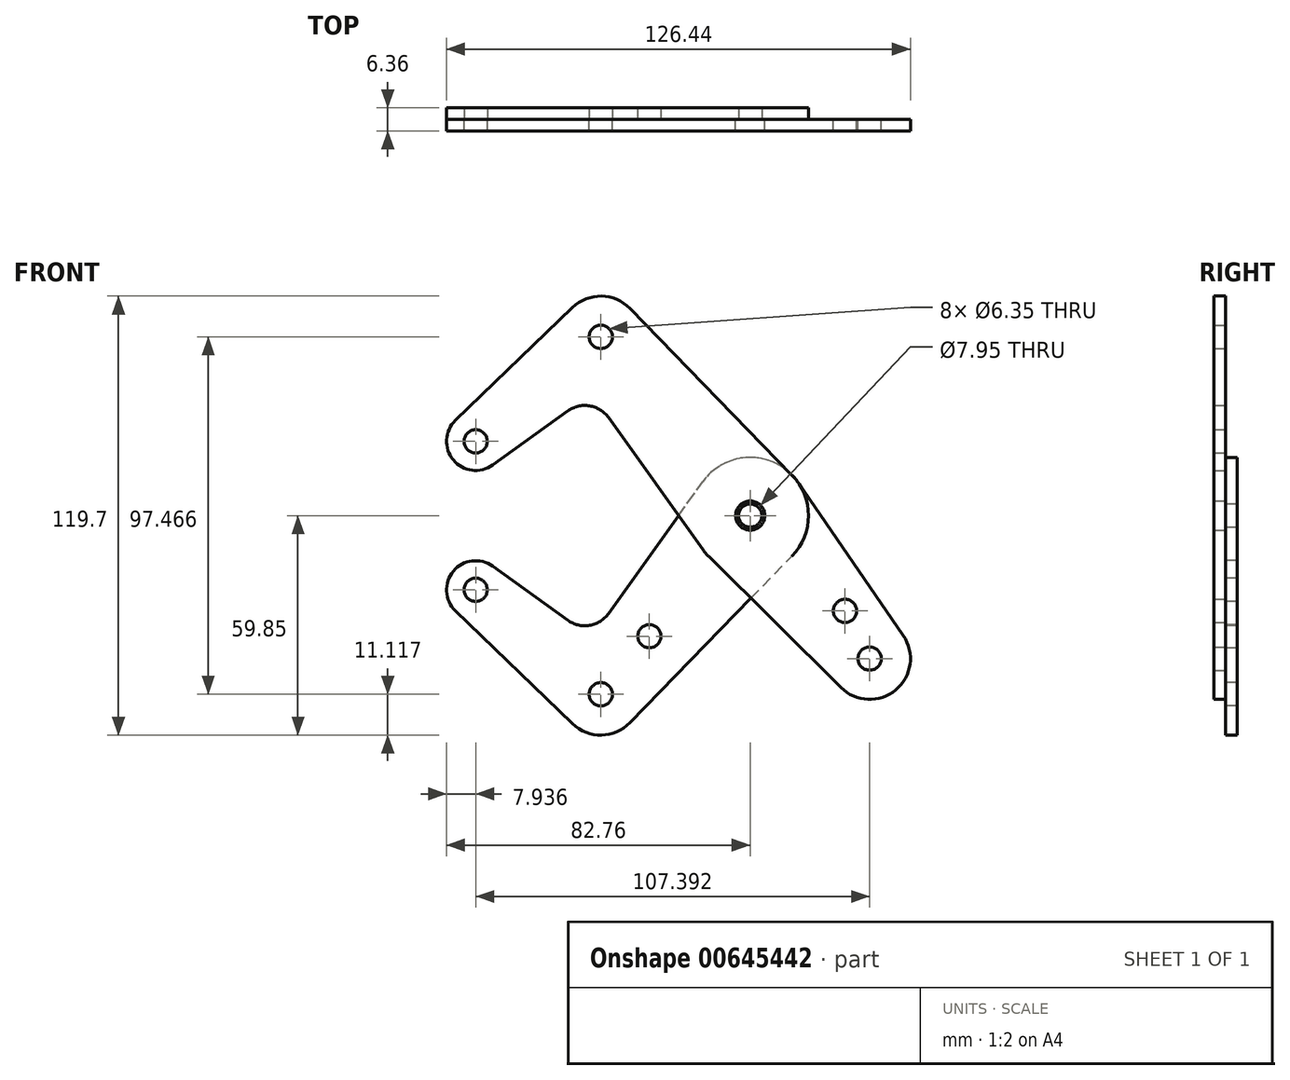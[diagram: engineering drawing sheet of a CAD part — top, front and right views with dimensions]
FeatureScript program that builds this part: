
annotation { "Feature Type Name" : "Feature", "Feature Type Description" : "" }
export const myFeature = defineFeature(function(context is Context, id is Id, definition is map)
    precondition{}
    {
        {
            var Q0;
            Q0=qCreatedBy(makeId("Front.planeOp"),FACE);
            var sketch = newSketch(context, id + "F0", { "sketchPlane" : qUnion([Q0])});
            skLineSegment(sketch, "E0", {"start": v(-74.82, 20.24) * mm, "end": v(-40.71, 48.73) * mm, "construction": true});
            skLineSegment(sketch, "E1", {"start": v(-40.71, 48.73) * mm, "end": v(32.57, -38.99) * mm, "construction": true});
            skCircle(sketch, "E2", {"center": v(-74.82, 20.24) * mm, "radius": 7.94 * mm});
            skCircle(sketch, "E3", {"center": v(-74.82, 20.24) * mm, "radius": 3.18 * mm});
            skCircle(sketch, "E4", {"center": v(-40.71, 48.73) * mm, "radius": 11.11 * mm});
            skCircle(sketch, "E5", {"center": v(-40.71, 48.73) * mm, "radius": 3.18 * mm});
            skCircle(sketch, "E6", {"center": v(0, 0) * mm, "radius": 15.88 * mm});
            skCircle(sketch, "E7", {"center": v(0, 0) * mm, "radius": 3.98 * mm});
            skCircle(sketch, "E8", {"center": v(0, 0) * mm, "radius": 3.18 * mm});
            skCircle(sketch, "E9", {"center": v(32.57, -38.99) * mm, "radius": 11.11 * mm});
            skCircle(sketch, "E10", {"center": v(32.57, -38.99) * mm, "radius": 3.18 * mm});
            skCircle(sketch, "E11", {"center": v(25.85, -26) * mm, "radius": 3.17 * mm});
            skLineSegment(sketch, "E12", {"start": v(-80.33, 25.95) * mm, "end": v(-48.43, 56.73) * mm});
            skLineSegment(sketch, "E13", {"start": v(-70.18, 13.8) * mm, "end": v(-49.73, 28.53) * mm});
            skLineSegment(sketch, "E14", {"start": v(-32.74, 56.48) * mm, "end": v(11.39, 11.06) * mm});
            skLineSegment(sketch, "E15", {"start": v(-38.62, 26.7) * mm, "end": v(-12.91, -9.24) * mm});
            skLineSegment(sketch, "E16", {"start": v(41.73, -32.7) * mm, "end": v(13.08, 9) * mm});
            skLineSegment(sketch, "E17", {"start": v(24.75, -46.88) * mm, "end": v(-11.18, -11.28) * mm});
            skArc(sketch, "E18.filletArc", {"start": v(-38.62, 26.7) * mm, "mid": v(-43.8, 29.93) * mm, "end": v(-49.73, 28.53) * mm});
            skLineSegment(sketch, "E19", {"start": v(0, 0) * mm, "end": v(-40.71, -48.73) * mm, "construction": true});
            skLineSegment(sketch, "E20", {"start": v(-40.71, -48.73) * mm, "end": v(-74.82, -20.24) * mm, "construction": true});
            skCircle(sketch, "E21", {"center": v(-74.82, -20.24) * mm, "radius": 7.94 * mm});
            skCircle(sketch, "E22", {"center": v(-74.82, -20.24) * mm, "radius": 3.18 * mm});
            skCircle(sketch, "E23", {"center": v(-40.71, -48.73) * mm, "radius": 11.11 * mm});
            skCircle(sketch, "E24", {"center": v(-40.71, -48.73) * mm, "radius": 3.17 * mm});
            skCircle(sketch, "E25", {"center": v(-27.47, -32.88) * mm, "radius": 3.18 * mm});
            skLineSegment(sketch, "E26", {"start": v(-80.33, -25.95) * mm, "end": v(-48.43, -56.73) * mm});
            skLineSegment(sketch, "E27", {"start": v(-70.18, -13.8) * mm, "end": v(-49.73, -28.53) * mm});
            skLineSegment(sketch, "E28", {"start": v(-38.62, -26.7) * mm, "end": v(-12.91, 9.24) * mm});
            skPoint(sketch, "E28.endSnap0", {"position": v(-25.77, 8.74) * mm});
            skLineSegment(sketch, "E29", {"start": v(-32.74, -56.48) * mm, "end": v(11.39, -11.06) * mm});
            skArc(sketch, "E30.filletArc", {"start": v(-49.73, -28.53) * mm, "mid": v(-43.8, -29.93) * mm, "end": v(-38.62, -26.7) * mm});
            skSolve(sketch);
        }
        {
            var Q0;
            {var subQ0=sQuery(id+"F0.wireOp",EDGE,"E12");Q0=makeQuery(id+"F0.imprint","IMPRINT",FACE,{"disambiguationData":[TD([[makeQuery(id+"F0.imprint","IMPRINT",EDGE,{"derivedFrom":subQ0}),-1.0]])]});}
            var Q1;
            {var subQ0=sQuery(id+"F0.wireOp",EDGE,"E17");var subQ1=sQuery(id+"F0.wireOp",EDGE,"E6");var subQ2=makeQuery(id+"F0.imprint","INTERSECT",VERTEX,{"derivedFrom":[subQ1,subQ0]});Q1=makeQuery(id+"F0.imprint","IMPRINT",FACE,{"disambiguationData":[TD([[makeQuery(id+"F0.imprint","IMPRINT",EDGE,{"disambiguationData":[TD([[subQ2,-1.0]])],"derivedFrom":subQ1}),-1.0]])]});}
            var Q2;
            Q2=makeQuery(id+"F0.imprint","IMPRINT",FACE,{"disambiguationData":[TD([[makeQuery(id+"F0.imprint","IMPRINT",EDGE,{"derivedFrom":sQuery(id+"F0.wireOp",EDGE,"E11")}),-1.0]])]});
            var Q3;
            Q3=makeQuery(id+"F0.imprint","IMPRINT",FACE,{"disambiguationData":[TD([[makeQuery(id+"F0.imprint","IMPRINT",EDGE,{"derivedFrom":sQuery(id+"F0.wireOp",EDGE,"E10")}),-1.0]])]});
            var Q4;
            Q4=makeQuery(id+"F0.imprint","IMPRINT",FACE,{"disambiguationData":[TD([[makeQuery(id+"F0.imprint","IMPRINT",EDGE,{"derivedFrom":sQuery(id+"F0.wireOp",EDGE,"E5")}),-1.0]])]});
            var Q5;
            Q5=makeQuery(id+"F0.imprint","IMPRINT",FACE,{"disambiguationData":[TD([[makeQuery(id+"F0.imprint","IMPRINT",EDGE,{"derivedFrom":sQuery(id+"F0.wireOp",EDGE,"E3")}),-1.0]])]});
            var Q6;
            Q6=makeQuery(id+"F0.imprint","IMPRINT",FACE,{"disambiguationData":[TD([[makeQuery(id+"F0.imprint","IMPRINT",EDGE,{"derivedFrom":sQuery(id+"F0.wireOp",EDGE,"E7")}),-1.0]])]});
            var Q7;
            {var subQ0=sQuery(id+"F0.wireOp",EDGE,"E15");var subQ1=sQuery(id+"F0.wireOp",EDGE,"E6");var subQ2=makeQuery(id+"F0.imprint","INTERSECT",VERTEX,{"derivedFrom":[subQ1,subQ0]});Q7=makeQuery(id+"F0.imprint","IMPRINT",FACE,{"disambiguationData":[TD([[makeQuery(id+"F0.imprint","IMPRINT",EDGE,{"disambiguationData":[TD([[subQ2,1.0]])],"derivedFrom":subQ1}),-1.0]])]});}
            extrude(context, id + "F1", {"entities" : qUnion([Q0, Q1, Q2, Q3, Q4, Q5, Q6, Q7]), "depth" : 3.17 * mm, "offsetDistance" : 25.4 * mm});
        }
        {
            var Q0;
            Q0=makeQuery(id+"F0.imprint","IMPRINT",FACE,{"disambiguationData":[TD([[makeQuery(id+"F0.imprint","IMPRINT",EDGE,{"derivedFrom":sQuery(id+"F0.wireOp",EDGE,"E22")}),-1.0]])]});
            var Q1;
            Q1=makeQuery(id+"F0.imprint","IMPRINT",FACE,{"disambiguationData":[TD([[makeQuery(id+"F0.imprint","IMPRINT",EDGE,{"derivedFrom":sQuery(id+"F0.wireOp",EDGE,"E25")}),-1.0]])]});
            var Q2;
            Q2=makeQuery(id+"F0.imprint","IMPRINT",FACE,{"disambiguationData":[TD([[makeQuery(id+"F0.imprint","IMPRINT",EDGE,{"derivedFrom":sQuery(id+"F0.wireOp",EDGE,"E24")}),-1.0]])]});
            var Q3;
            {var subQ0=sQuery(id+"F0.wireOp",EDGE,"E15");var subQ1=sQuery(id+"F0.wireOp",EDGE,"E6");var subQ2=makeQuery(id+"F0.imprint","INTERSECT",VERTEX,{"derivedFrom":[subQ1,subQ0]});Q3=makeQuery(id+"F0.imprint","IMPRINT",FACE,{"disambiguationData":[TD([[makeQuery(id+"F0.imprint","IMPRINT",EDGE,{"disambiguationData":[TD([[subQ2,1.0]])],"derivedFrom":subQ1}),-1.0]])]});}
            var Q4;
            {var subQ0=sQuery(id+"F0.wireOp",EDGE,"E17");var subQ1=sQuery(id+"F0.wireOp",EDGE,"E6");var subQ2=makeQuery(id+"F0.imprint","INTERSECT",VERTEX,{"derivedFrom":[subQ1,subQ0]});Q4=makeQuery(id+"F0.imprint","IMPRINT",FACE,{"disambiguationData":[TD([[makeQuery(id+"F0.imprint","IMPRINT",EDGE,{"disambiguationData":[TD([[subQ2,-1.0]])],"derivedFrom":subQ1}),-1.0]])]});}
            var Q5;
            Q5=makeQuery(id+"F0.imprint","IMPRINT",FACE,{"disambiguationData":[TD([[makeQuery(id+"F0.imprint","IMPRINT",EDGE,{"derivedFrom":sQuery(id+"F0.wireOp",EDGE,"E7")}),-1.0]])]});
            var Q6;
            Q6=makeQuery(id+"F0.imprint","IMPRINT",FACE,{"disambiguationData":[TD([[makeQuery(id+"F0.imprint","IMPRINT",EDGE,{"derivedFrom":sQuery(id+"F0.wireOp",EDGE,"E7")}),1.0]])]});
            extrude(context, id + "F2", {"entities" : qUnion([Q0, Q1, Q2, Q3, Q4, Q5, Q6]), "oppositeDirection" : true, "depth" : 3.17 * mm, "offsetDistance" : 25.4 * mm});
        }
    });
